# Revit family: SANINDUSA_110034004_Cetus_Cetusrimflushwallmountedwc370x529x380_V0
name_source: partatom
category: Plumbing Fixtures
revit_build: Autodesk Revit 2018 (Build: 20170223_1515(x64)
units: mm (PartAtom-declared; Revit-internal decimal feet)

## family parameters
Cut with Voids When Loaded = No
Host = Face
Part Type = Normal
Room Calculation Point = No
Round Connector Dimension = Use Diameter
Shared = No

## types (1)
- SANINDUSA_110034004_Cetus_Cetusrimflushwallmountedwc370x529x380_V0
    AssetType = Fixed
    CodePerformance = EN 997:2012  CL 1 - 6 A
    Color = white
    Constituents = Compatible toilet seats (not included):21031 - Cetus toilet seat with clipoff and slowclose system; 21011 - Cetus toilet seat with clipoff system; 21021 - Cetus toilet seat with clipoff; 21061 - Cetus toilet seat with clipoff and slowclose system; 41733xx ‐ SANGLASS WALL external frame w/ dual flushing cistern for wall hung WC; 4193311 – Pack SANSLIM built‐in frame w/ dual flushing cistern for wall hung WC + To‐Slim dual flush plate; 411023 ‐ SANDOUBLE free standing frame w/ dual flushing cistern for wall hung WC; 4103311 ‐ Moove dual flush plate; 40333 ‐ SANFIX frame w/ dual flushing cistern for wall hung WC (for brick walls); 40323 ‐ SANFIX free standing frame w/ dual flushing cistern for wall hung WC; 40233 ‐ SANFLUSH built‐in frame w/ dual flushing cistern for wall hung WC; 40633 ‐ SANSPACE frame w/ dual flushing cistern for wall hung WC; (for brick walls); 40533 ‐ SANBEST built‐in frame w/ dual flushing cistern for wall hung WC (for brick walls); 40003xx ‐ Orange dual flush plate; 40013xx ‐ Plan dual flush plate; 40023xx‐ Easy dual flush plate; 40033xx – Moon dual flush plate; 40043xx – Square dual flush plate;
    Default Elevation = 1219 mm
    Description = Soil appliance for the disposal of excrement.
    DrainSize = 100 mm  [stored 0.328084 ft]
    Element Type = TOILETPAN: Soil appliance for the disposal of excrement.
    Features = "Domestic and commercial use. With rimflush discharge system without rim, which promotes hygiene,
make easier the toilet cleaning and reduces the proliferation of germs. Toilet seat with clipoff system easy to clean and slow close. Without holes in the sidewalls. Invisible fixation"
    Finish = gloss
    InletDiameter = 0 mm  [stored 0 ft]
    Installation Instructions = https://www.tec.sanindusa.pt
    Manufacturer = Sanindusa
    ManufacturerName = Sanindusa
    ManufacturerURL = www.tec.sanindusa.pt
    Material = vitreous china
    Model = 110034004
    ModelNumber = 110034004
    ModelReference = Cetus
    Name = Cetus rimflush wall mounted wc
    NominalHeight = 380 mm
    NominalLength = 370 mm  [stored 1.21391 ft]
    NominalWidth = 529 mm  [stored 1.73556 ft]
    PanColor = white
    PanMaterial = vitreous china
    PanMounting = wallhung
    Pre-defined type (IFC) = TOILETPAN
    ProductInformation = https://www.tec.sanindusa.pt
    ProductionYear = 2016
    Size = 370x529x380
    ToiletPanType = washdown
    ToiletType = LooseCoupled
    Type (IFC) = IfcSanitaryTerminalType
    URL = www.tec.sanindusa.pt
    Version = 1
    WarrantyDescription = https://www.tec.sanindusa.pt
    WarrantyDurationParts = 5
    WarrantyDurationUnit = year
    Waste Connection = Yes
    Weight = 15.30 kg

note: [stored X ft] marks values corroborated as IEEE doubles in the binary element streams (Revit-internal decimal feet)

## geometry (parser evidence)
native form markers: Sweep x5
no freeform markers — native parametric forms only
